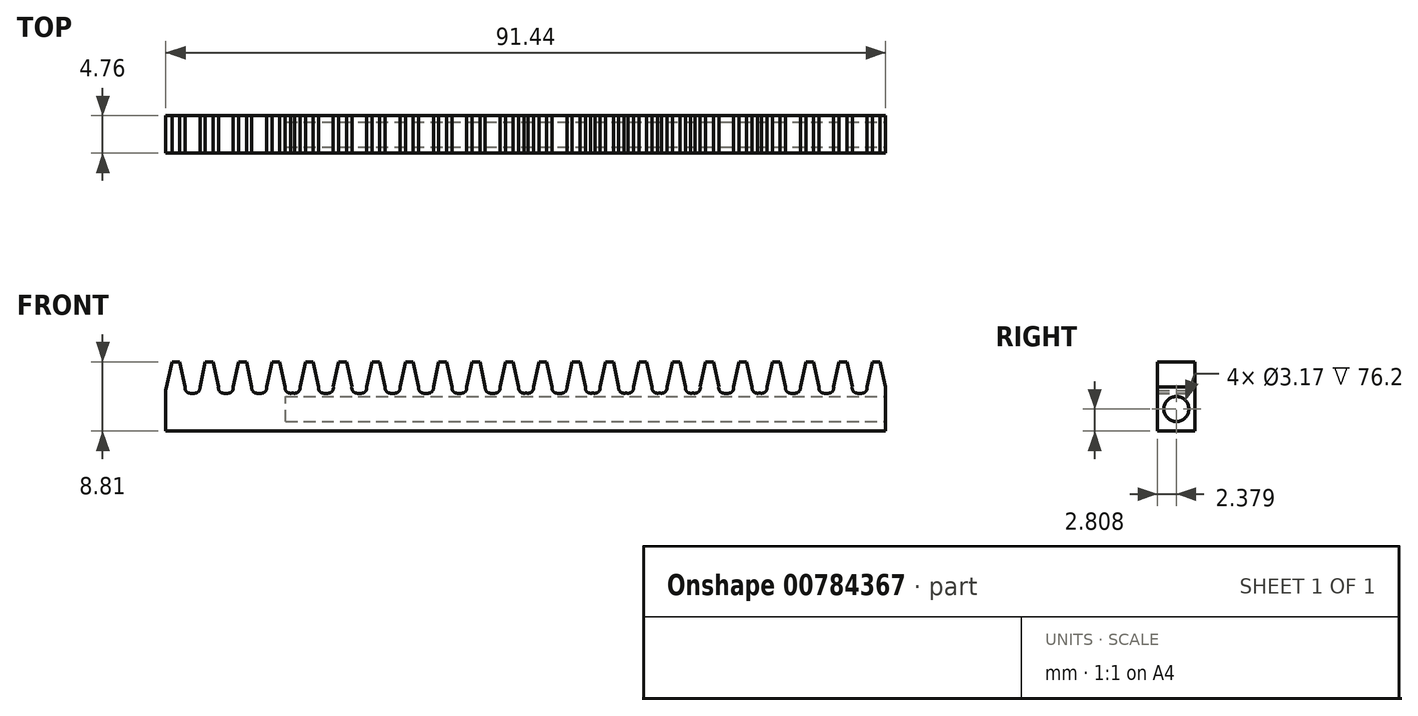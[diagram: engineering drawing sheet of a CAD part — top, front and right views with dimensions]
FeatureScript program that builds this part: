
annotation { "Feature Type Name" : "Feature", "Feature Type Description" : "" }
export const myFeature = defineFeature(function(context is Context, id is Id, definition is map)
    precondition{}
    {
        {
            var Q0;
            Q0=qCreatedBy(makeId("Front.planeOp"),FACE);
            var sketch = newSketch(context, id + "F0", { "sketchPlane" : qUnion([Q0])});
            skArc(sketch, "E0.0", {"start": v(-35.96, 4.83) * mm, "mid": v(-36.44, 4.85) * mm, "end": v(-36.93, 4.83) * mm});
            skArc(sketch, "E1.0", {"start": v(-35.27, 1.66) * mm, "mid": v(-35.12, 1.1) * mm, "end": v(-34.6, 0.86) * mm});
            skArc(sketch, "E2.0", {"start": v(-31.72, 4.83) * mm, "mid": v(-32.2, 4.85) * mm, "end": v(-32.7, 4.83) * mm});
            skArc(sketch, "E3.0", {"start": v(-31.03, 1.66) * mm, "mid": v(-30.88, 1.1) * mm, "end": v(-30.35, 0.86) * mm});
            skArc(sketch, "E4.0", {"start": v(-29.82, 0.86) * mm, "mid": v(-30.09, 0.86) * mm, "end": v(-30.35, 0.86) * mm});
            skArc(sketch, "E5.0", {"start": v(-27.48, 4.83) * mm, "mid": v(-27.97, 4.85) * mm, "end": v(-28.46, 4.83) * mm});
            skArc(sketch, "E6.0", {"start": v(-29.82, 0.86) * mm, "mid": v(-29.3, 1.1) * mm, "end": v(-29.15, 1.66) * mm});
            skArc(sketch, "E7.0", {"start": v(-26.8, 1.66) * mm, "mid": v(-26.64, 1.1) * mm, "end": v(-26.12, 0.86) * mm});
            skArc(sketch, "E8.0", {"start": v(-25.58, 0.86) * mm, "mid": v(-25.85, 0.86) * mm, "end": v(-26.12, 0.86) * mm});
            skArc(sketch, "E9.0", {"start": v(-34.06, 0.86) * mm, "mid": v(-34.32, 0.86) * mm, "end": v(-34.6, 0.86) * mm});
            skArc(sketch, "E10.0", {"start": v(-34.06, 0.86) * mm, "mid": v(-33.53, 1.1) * mm, "end": v(-33.38, 1.66) * mm});
            skArc(sketch, "E11.0", {"start": v(-23.24, 4.83) * mm, "mid": v(-23.73, 4.85) * mm, "end": v(-24.22, 4.83) * mm});
            skArc(sketch, "E12.0", {"start": v(-25.58, 0.86) * mm, "mid": v(-25.06, 1.1) * mm, "end": v(-24.91, 1.66) * mm});
            skArc(sketch, "E13.0", {"start": v(-22.55, 1.66) * mm, "mid": v(-22.4, 1.1) * mm, "end": v(-21.88, 0.86) * mm});
            skArc(sketch, "E14.0", {"start": v(-19, 4.83) * mm, "mid": v(-19.5, 4.85) * mm, "end": v(-19.98, 4.83) * mm});
            skArc(sketch, "E15.0", {"start": v(-18.32, 1.66) * mm, "mid": v(-18.17, 1.1) * mm, "end": v(-17.64, 0.86) * mm});
            skArc(sketch, "E16.0", {"start": v(-17.1, 0.86) * mm, "mid": v(-17.38, 0.86) * mm, "end": v(-17.64, 0.86) * mm});
            skArc(sketch, "E17.0", {"start": v(-14.77, 4.83) * mm, "mid": v(-15.26, 4.85) * mm, "end": v(-15.74, 4.83) * mm});
            skArc(sketch, "E18.0", {"start": v(-17.1, 0.86) * mm, "mid": v(-16.59, 1.1) * mm, "end": v(-16.44, 1.66) * mm});
            skArc(sketch, "E19.0", {"start": v(-14.08, 1.66) * mm, "mid": v(-13.93, 1.1) * mm, "end": v(-13.4, 0.86) * mm});
            skArc(sketch, "E20.0", {"start": v(-12.87, 0.86) * mm, "mid": v(-13.14, 0.86) * mm, "end": v(-13.4, 0.86) * mm});
            skArc(sketch, "E21.0", {"start": v(-21.35, 0.86) * mm, "mid": v(-21.61, 0.86) * mm, "end": v(-21.88, 0.86) * mm});
            skArc(sketch, "E22.0", {"start": v(-21.35, 0.86) * mm, "mid": v(-20.82, 1.1) * mm, "end": v(-20.67, 1.66) * mm});
            skArc(sketch, "E23.0", {"start": v(-12.87, 0.86) * mm, "mid": v(-12.35, 1.1) * mm, "end": v(-12.2, 1.66) * mm});
            skArc(sketch, "E24.0", {"start": v(-10.53, 4.83) * mm, "mid": v(-11.02, 4.85) * mm, "end": v(-11.5, 4.83) * mm});
            skArc(sketch, "E25.0", {"start": v(-9.84, 1.66) * mm, "mid": v(-9.7, 1.1) * mm, "end": v(-9.17, 0.86) * mm});
            skArc(sketch, "E26.0", {"start": v(-6.3, 4.83) * mm, "mid": v(-6.78, 4.85) * mm, "end": v(-7.27, 4.83) * mm});
            skArc(sketch, "E27.0", {"start": v(-5.6, 1.66) * mm, "mid": v(-5.45, 1.1) * mm, "end": v(-4.93, 0.86) * mm});
            skArc(sketch, "E28.0", {"start": v(-4.4, 0.86) * mm, "mid": v(-4.66, 0.86) * mm, "end": v(-4.93, 0.86) * mm});
            skArc(sketch, "E29.0", {"start": v(-2.06, 4.83) * mm, "mid": v(-2.54, 4.85) * mm, "end": v(-3.03, 4.83) * mm});
            skArc(sketch, "E30.0", {"start": v(-4.4, 0.86) * mm, "mid": v(-3.87, 1.1) * mm, "end": v(-3.72, 1.66) * mm});
            skArc(sketch, "E31.0", {"start": v(-1.37, 1.66) * mm, "mid": v(-1.22, 1.1) * mm, "end": v(-0.7, 0.86) * mm});
            skArc(sketch, "E32.0", {"start": v(-0.16, 0.86) * mm, "mid": v(-0.43, 0.86) * mm, "end": v(-0.7, 0.86) * mm});
            skArc(sketch, "E33.0", {"start": v(-8.63, 0.86) * mm, "mid": v(-8.9, 0.86) * mm, "end": v(-9.17, 0.86) * mm});
            skArc(sketch, "E34.0", {"start": v(-8.63, 0.86) * mm, "mid": v(-8.11, 1.1) * mm, "end": v(-7.96, 1.66) * mm});
            skArc(sketch, "E35.0", {"start": v(2.18, 4.83) * mm, "mid": v(1.7, 4.85) * mm, "end": v(1.2, 4.83) * mm});
            skArc(sketch, "E36.0", {"start": v(-0.16, 0.86) * mm, "mid": v(0.36, 1.1) * mm, "end": v(0.51, 1.66) * mm});
            skArc(sketch, "E37.0", {"start": v(2.87, 1.66) * mm, "mid": v(3.02, 1.1) * mm, "end": v(3.54, 0.86) * mm});
            skArc(sketch, "E38.0", {"start": v(6.42, 4.83) * mm, "mid": v(5.93, 4.85) * mm, "end": v(5.44, 4.83) * mm});
            skArc(sketch, "E39.0", {"start": v(7.1, 1.66) * mm, "mid": v(7.26, 1.1) * mm, "end": v(7.78, 0.86) * mm});
            skArc(sketch, "E40.0", {"start": v(8.32, 0.86) * mm, "mid": v(8.05, 0.86) * mm, "end": v(7.78, 0.86) * mm});
            skArc(sketch, "E41.0", {"start": v(10.65, 4.83) * mm, "mid": v(10.17, 4.85) * mm, "end": v(9.68, 4.83) * mm});
            skArc(sketch, "E42.0", {"start": v(11.35, 1.66) * mm, "mid": v(11.5, 1.1) * mm, "end": v(12.02, 0.86) * mm});
            skArc(sketch, "E43.0", {"start": v(4.08, 0.86) * mm, "mid": v(3.81, 0.86) * mm, "end": v(3.54, 0.86) * mm});
            skArc(sketch, "E44.0", {"start": v(4.08, 0.86) * mm, "mid": v(4.6, 1.1) * mm, "end": v(4.75, 1.66) * mm});
            skLineSegment(sketch, "E45.top", {"start": v(53.72, -3.96) * mm, "end": v(-37.72, -3.96) * mm});
            skLineSegment(sketch, "E45.right", {"start": v(-37.72, 1.2) * mm, "end": v(-37.72, -3.96) * mm});
            skLineSegment(sketch, "E46.trimOffspring", {"start": v(-34.06, 0.86) * mm, "end": v(-34.6, 0.86) * mm});
            skLineSegment(sketch, "E47.trimOffspring", {"start": v(-29.82, 0.86) * mm, "end": v(-30.35, 0.86) * mm});
            skLineSegment(sketch, "E48.trimOffspring", {"start": v(-25.58, 0.86) * mm, "end": v(-26.12, 0.86) * mm});
            skLineSegment(sketch, "E49.trimOffspring", {"start": v(-17.1, 0.86) * mm, "end": v(-17.64, 0.86) * mm});
            skLineSegment(sketch, "E50.trimOffspring", {"start": v(-12.87, 0.86) * mm, "end": v(-13.4, 0.86) * mm});
            skLineSegment(sketch, "E51.trimOffspring", {"start": v(-8.63, 0.86) * mm, "end": v(-9.17, 0.86) * mm});
            skLineSegment(sketch, "E52.trimOffspring", {"start": v(-4.4, 0.86) * mm, "end": v(-4.93, 0.86) * mm});
            skLineSegment(sketch, "E53.trimOffspring", {"start": v(-0.16, 0.86) * mm, "end": v(-0.7, 0.86) * mm});
            skLineSegment(sketch, "E54.trimOffspring", {"start": v(4.08, 0.86) * mm, "end": v(3.54, 0.86) * mm});
            skLineSegment(sketch, "E55", {"start": v(-11.5, 4.83) * mm, "end": v(-12.2, 1.66) * mm});
            skLineSegment(sketch, "E56", {"start": v(-10.53, 4.83) * mm, "end": v(-9.84, 1.66) * mm});
            skLineSegment(sketch, "E57", {"start": v(-7.27, 4.83) * mm, "end": v(-7.96, 1.66) * mm});
            skLineSegment(sketch, "E58", {"start": v(-6.3, 4.83) * mm, "end": v(-5.6, 1.66) * mm});
            skLineSegment(sketch, "E59", {"start": v(-37.72, 1.2) * mm, "end": v(-36.93, 4.83) * mm});
            skLineSegment(sketch, "E60", {"start": v(-35.96, 4.83) * mm, "end": v(-35.27, 1.66) * mm});
            skLineSegment(sketch, "E61", {"start": v(-33.38, 1.66) * mm, "end": v(-32.7, 4.83) * mm});
            skLineSegment(sketch, "E62", {"start": v(-31.72, 4.83) * mm, "end": v(-31.03, 1.66) * mm});
            skLineSegment(sketch, "E63", {"start": v(-29.15, 1.66) * mm, "end": v(-28.46, 4.83) * mm});
            skLineSegment(sketch, "E64", {"start": v(-27.48, 4.83) * mm, "end": v(-26.8, 1.66) * mm});
            skLineSegment(sketch, "E65", {"start": v(-24.91, 1.66) * mm, "end": v(-24.22, 4.83) * mm});
            skLineSegment(sketch, "E66", {"start": v(-23.24, 4.83) * mm, "end": v(-22.55, 1.66) * mm});
            skLineSegment(sketch, "E67", {"start": v(-20.67, 1.66) * mm, "end": v(-19.98, 4.83) * mm});
            skLineSegment(sketch, "E68", {"start": v(-19, 4.83) * mm, "end": v(-18.32, 1.66) * mm});
            skLineSegment(sketch, "E69", {"start": v(-14.77, 4.83) * mm, "end": v(-14.08, 1.66) * mm});
            skLineSegment(sketch, "E70", {"start": v(-3.72, 1.66) * mm, "end": v(-3.03, 4.83) * mm});
            skLineSegment(sketch, "E71", {"start": v(-2.06, 4.83) * mm, "end": v(-1.37, 1.66) * mm});
            skLineSegment(sketch, "E72", {"start": v(0.51, 1.66) * mm, "end": v(1.2, 4.83) * mm});
            skLineSegment(sketch, "E73", {"start": v(2.18, 4.83) * mm, "end": v(2.87, 1.66) * mm});
            skLineSegment(sketch, "E74", {"start": v(4.75, 1.66) * mm, "end": v(5.44, 4.83) * mm});
            skLineSegment(sketch, "E75", {"start": v(6.42, 4.83) * mm, "end": v(7.1, 1.66) * mm});
            skLineSegment(sketch, "E76", {"start": v(-16.44, 1.66) * mm, "end": v(-15.74, 4.83) * mm});
            skArc(sketch, "E77.0", {"start": v(8.32, 0.86) * mm, "mid": v(8.84, 1.1) * mm, "end": v(8.99, 1.66) * mm});
            skArc(sketch, "E78.0", {"start": v(14.9, 4.83) * mm, "mid": v(14.4, 4.85) * mm, "end": v(13.92, 4.83) * mm});
            skArc(sketch, "E79.0", {"start": v(15.58, 1.66) * mm, "mid": v(15.73, 1.1) * mm, "end": v(16.26, 0.86) * mm});
            skArc(sketch, "E80.0", {"start": v(16.79, 0.86) * mm, "mid": v(16.52, 0.86) * mm, "end": v(16.26, 0.86) * mm});
            skArc(sketch, "E81.0", {"start": v(19.13, 4.83) * mm, "mid": v(18.64, 4.85) * mm, "end": v(18.15, 4.83) * mm});
            skArc(sketch, "E82.0", {"start": v(16.79, 0.86) * mm, "mid": v(17.31, 1.1) * mm, "end": v(17.46, 1.66) * mm});
            skArc(sketch, "E83.0", {"start": v(19.82, 1.66) * mm, "mid": v(19.97, 1.1) * mm, "end": v(20.5, 0.86) * mm});
            skArc(sketch, "E84.0", {"start": v(21.03, 0.86) * mm, "mid": v(20.76, 0.86) * mm, "end": v(20.5, 0.86) * mm});
            skArc(sketch, "E85.0", {"start": v(12.55, 0.86) * mm, "mid": v(13.08, 1.1) * mm, "end": v(13.23, 1.66) * mm});
            skArc(sketch, "E86.0", {"start": v(23.37, 4.83) * mm, "mid": v(22.88, 4.85) * mm, "end": v(22.4, 4.83) * mm});
            skArc(sketch, "E87.0", {"start": v(21.03, 0.86) * mm, "mid": v(21.55, 1.1) * mm, "end": v(21.7, 1.66) * mm});
            skArc(sketch, "E88.0", {"start": v(24.06, 1.66) * mm, "mid": v(24.2, 1.1) * mm, "end": v(24.73, 0.86) * mm});
            skArc(sketch, "E89.0", {"start": v(27.6, 4.83) * mm, "mid": v(27.12, 4.85) * mm, "end": v(26.63, 4.83) * mm});
            skArc(sketch, "E90.0", {"start": v(28.3, 1.66) * mm, "mid": v(28.44, 1.1) * mm, "end": v(28.97, 0.86) * mm});
            skArc(sketch, "E91.0", {"start": v(29.5, 0.86) * mm, "mid": v(29.23, 0.86) * mm, "end": v(28.97, 0.86) * mm});
            skArc(sketch, "E92.0", {"start": v(31.84, 4.83) * mm, "mid": v(31.35, 4.85) * mm, "end": v(30.87, 4.83) * mm});
            skArc(sketch, "E93.0", {"start": v(29.5, 0.86) * mm, "mid": v(30.03, 1.1) * mm, "end": v(30.18, 1.66) * mm});
            skArc(sketch, "E94.0", {"start": v(32.53, 1.66) * mm, "mid": v(32.68, 1.1) * mm, "end": v(33.2, 0.86) * mm});
            skArc(sketch, "E95.0", {"start": v(25.26, 0.86) * mm, "mid": v(25, 0.86) * mm, "end": v(24.73, 0.86) * mm});
            skArc(sketch, "E96.0", {"start": v(25.26, 0.86) * mm, "mid": v(25.79, 1.1) * mm, "end": v(25.94, 1.66) * mm});
            skArc(sketch, "E97.0", {"start": v(33.74, 0.86) * mm, "mid": v(34.26, 1.1) * mm, "end": v(34.41, 1.66) * mm});
            skArc(sketch, "E98.0", {"start": v(36.08, 4.83) * mm, "mid": v(35.6, 4.85) * mm, "end": v(35.1, 4.83) * mm});
            skArc(sketch, "E99.0", {"start": v(36.77, 1.66) * mm, "mid": v(36.92, 1.1) * mm, "end": v(37.44, 0.86) * mm});
            skArc(sketch, "E100.0", {"start": v(40.32, 4.83) * mm, "mid": v(39.83, 4.85) * mm, "end": v(39.34, 4.83) * mm});
            skArc(sketch, "E101.0", {"start": v(41, 1.66) * mm, "mid": v(41.16, 1.1) * mm, "end": v(41.68, 0.86) * mm});
            skArc(sketch, "E102.0", {"start": v(44.55, 4.83) * mm, "mid": v(44.07, 4.85) * mm, "end": v(43.58, 4.83) * mm});
            skArc(sketch, "E103.0", {"start": v(42.21, 0.86) * mm, "mid": v(42.74, 1.1) * mm, "end": v(42.89, 1.66) * mm});
            skArc(sketch, "E104.0", {"start": v(45.24, 1.66) * mm, "mid": v(45.4, 1.1) * mm, "end": v(45.92, 0.86) * mm});
            skArc(sketch, "E105.0", {"start": v(37.98, 0.86) * mm, "mid": v(37.7, 0.86) * mm, "end": v(37.44, 0.86) * mm});
            skArc(sketch, "E106.0", {"start": v(37.98, 0.86) * mm, "mid": v(38.5, 1.1) * mm, "end": v(38.65, 1.66) * mm});
            skLineSegment(sketch, "E107.trimOffspring", {"start": v(12.55, 0.86) * mm, "end": v(12.02, 0.86) * mm});
            skLineSegment(sketch, "E108.trimOffspring", {"start": v(33.74, 0.86) * mm, "end": v(33.2, 0.86) * mm});
            skLineSegment(sketch, "E109.trimOffspring", {"start": v(42.21, 0.86) * mm, "end": v(41.68, 0.86) * mm});
            skLineSegment(sketch, "E110.trimOffspring", {"start": v(46.45, 0.86) * mm, "end": v(45.92, 0.86) * mm});
            skLineSegment(sketch, "E111", {"start": v(35.1, 4.83) * mm, "end": v(34.41, 1.66) * mm});
            skLineSegment(sketch, "E112", {"start": v(36.08, 4.83) * mm, "end": v(36.77, 1.66) * mm});
            skLineSegment(sketch, "E113", {"start": v(39.34, 4.83) * mm, "end": v(38.65, 1.66) * mm});
            skLineSegment(sketch, "E114", {"start": v(40.32, 4.83) * mm, "end": v(41, 1.66) * mm});
            skLineSegment(sketch, "E115", {"start": v(8.99, 1.66) * mm, "end": v(9.68, 4.83) * mm});
            skLineSegment(sketch, "E116", {"start": v(10.65, 4.83) * mm, "end": v(11.35, 1.66) * mm});
            skLineSegment(sketch, "E117", {"start": v(13.23, 1.66) * mm, "end": v(13.92, 4.83) * mm});
            skLineSegment(sketch, "E118", {"start": v(14.9, 4.83) * mm, "end": v(15.58, 1.66) * mm});
            skLineSegment(sketch, "E119", {"start": v(17.46, 1.66) * mm, "end": v(18.15, 4.83) * mm});
            skLineSegment(sketch, "E120", {"start": v(19.13, 4.83) * mm, "end": v(19.82, 1.66) * mm});
            skLineSegment(sketch, "E121", {"start": v(21.7, 1.66) * mm, "end": v(22.4, 4.83) * mm});
            skLineSegment(sketch, "E122", {"start": v(23.37, 4.83) * mm, "end": v(24.06, 1.66) * mm});
            skLineSegment(sketch, "E123", {"start": v(25.94, 1.66) * mm, "end": v(26.63, 4.83) * mm});
            skLineSegment(sketch, "E124", {"start": v(27.6, 4.83) * mm, "end": v(28.3, 1.66) * mm});
            skLineSegment(sketch, "E125", {"start": v(31.84, 4.83) * mm, "end": v(32.53, 1.66) * mm});
            skLineSegment(sketch, "E126", {"start": v(42.89, 1.66) * mm, "end": v(43.58, 4.83) * mm});
            skLineSegment(sketch, "E127", {"start": v(44.55, 4.83) * mm, "end": v(45.24, 1.66) * mm});
            skLineSegment(sketch, "E128", {"start": v(30.18, 1.66) * mm, "end": v(30.87, 4.83) * mm});
            skArc(sketch, "E129.0", {"start": v(99.95, 6.75) * mm, "mid": v(99.47, 6.76) * mm, "end": v(98.98, 6.75) * mm});
            skArc(sketch, "E130.0", {"start": v(97.62, 2.77) * mm, "mid": v(98.14, 3.02) * mm, "end": v(98.29, 3.57) * mm});
            skArc(sketch, "E131.0", {"start": v(100.65, 3.57) * mm, "mid": v(100.8, 3.02) * mm, "end": v(101.32, 2.77) * mm});
            skLineSegment(sketch, "E132.trimOffspring", {"start": v(101.85, 2.77) * mm, "end": v(101.32, 2.77) * mm});
            skLineSegment(sketch, "E133", {"start": v(98.29, 3.57) * mm, "end": v(98.98, 6.75) * mm});
            skLineSegment(sketch, "E134", {"start": v(99.95, 6.75) * mm, "end": v(100.65, 3.57) * mm});
            skArc(sketch, "E135.0", {"start": v(48.8, 4.83) * mm, "mid": v(48.3, 4.85) * mm, "end": v(47.82, 4.83) * mm});
            skArc(sketch, "E136.0", {"start": v(46.45, 0.86) * mm, "mid": v(46.97, 1.1) * mm, "end": v(47.12, 1.66) * mm});
            skArc(sketch, "E137.0", {"start": v(49.48, 1.66) * mm, "mid": v(49.63, 1.1) * mm, "end": v(50.15, 0.86) * mm});
            skLineSegment(sketch, "E138.trimOffspring", {"start": v(50.69, 0.86) * mm, "end": v(50.15, 0.86) * mm});
            skLineSegment(sketch, "E139", {"start": v(47.12, 1.66) * mm, "end": v(47.82, 4.83) * mm});
            skLineSegment(sketch, "E140", {"start": v(48.8, 4.83) * mm, "end": v(49.48, 1.66) * mm});
            skArc(sketch, "E141.0", {"start": v(53.03, 4.83) * mm, "mid": v(52.54, 4.85) * mm, "end": v(52.05, 4.83) * mm});
            skArc(sketch, "E142.0", {"start": v(50.69, 0.86) * mm, "mid": v(51.21, 1.1) * mm, "end": v(51.36, 1.66) * mm});
            skLineSegment(sketch, "E143", {"start": v(51.36, 1.66) * mm, "end": v(52.05, 4.83) * mm});
            skLineSegment(sketch, "E144", {"start": v(53.03, 4.83) * mm, "end": v(53.72, 1.66) * mm});
            skLineSegment(sketch, "E145", {"start": v(53.72, -3.96) * mm, "end": v(53.72, 1.66) * mm});
            skSolve(sketch);
        }
        {
            var Q0;
            Q0=makeQuery(id+"F0.imprint","IMPRINT",FACE,{"disambiguationData":[TD([[makeQuery(id+"F0.imprint","IMPRINT",EDGE,{"derivedFrom":sQuery(id+"F0.wireOp",EDGE,"E0.0")}),1.0]])]});
            extrude(context, id + "F1", {"entities" : qUnion([Q0]), "depth" : 4.76 * mm, "offsetDistance" : 25.4 * mm});
        }
        {
            var Q0;
            Q0=makeQuery(id+"F1.opExtrude","SWEPT_FACE",FACE,{"disambiguationData":[OSD([sQuery(id+"F0.wireOp",EDGE,"E145")])]});
            var sketch = newSketch(context, id + "F2", { "sketchPlane" : qUnion([Q0])});
            skCircle(sketch, "E146", {"center": v(-2.38, -1.15) * mm, "radius": 1.59 * mm});
            skPoint(sketch, "E146.centerSnap0", {"position": v(0, -1.15) * mm});
            skPoint(sketch, "E146.centerSnap1", {"position": v(-2.38, -3.96) * mm});
            skSolve(sketch);
        }
        {
            var Q0;
            Q0=makeQuery(id+"F2.imprint","IMPRINT",FACE,{"disambiguationData":[TD([[makeQuery(id+"F2.imprint","IMPRINT",EDGE,{"derivedFrom":sQuery(id+"F2.wireOp",EDGE,"E146")}),1.0]])]});
            extrude(context, id + "F3", {"entities" : qUnion([Q0]), "operationType" : NewBodyOperationType.REMOVE, "oppositeDirection" : true, "depth" : 76.2 * mm, "offsetDistance" : 25.4 * mm});
        }
    });
